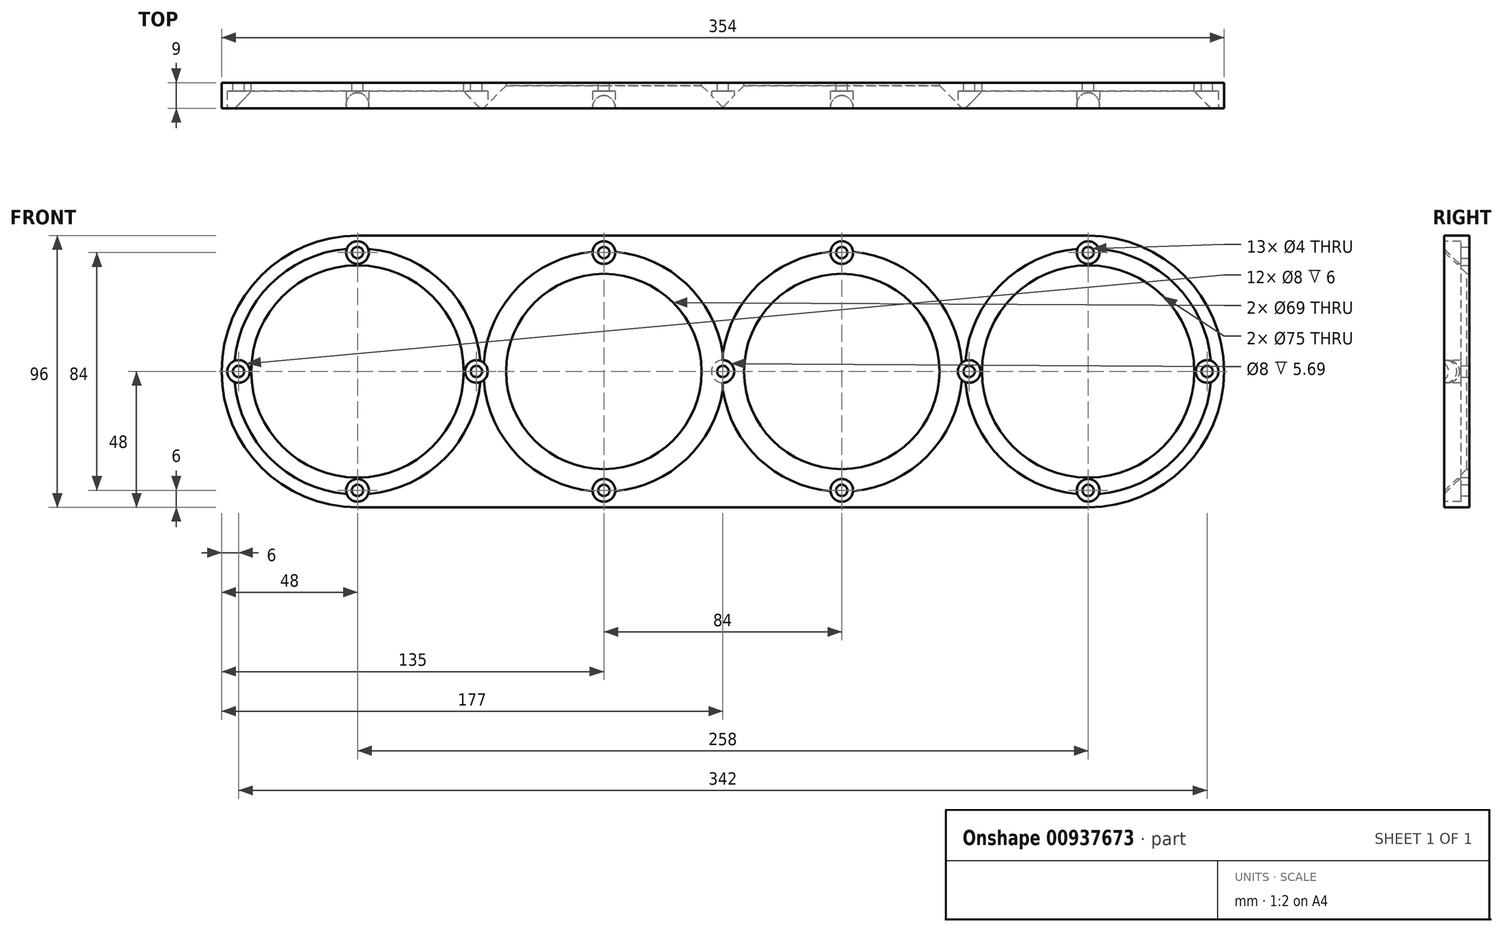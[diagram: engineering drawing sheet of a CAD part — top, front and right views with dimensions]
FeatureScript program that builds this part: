
annotation { "Feature Type Name" : "Feature", "Feature Type Description" : "" }
export const myFeature = defineFeature(function(context is Context, id is Id, definition is map)
    precondition{}
    {
        {
            var Q0;
            Q0=qCreatedBy(makeId("Front.planeOp"),FACE);
            var sketch = newSketch(context, id + "F0", { "sketchPlane" : qUnion([Q0])});
            skCircle(sketch, "E0", {"center": v(42, 0) * mm, "radius": 34.5 * mm});
            skCircle(sketch, "E1", {"center": v(129, 0) * mm, "radius": 37.5 * mm});
            skLineSegment(sketch, "E2", {"start": v(0, -113.77) * mm, "end": v(0, 113.17) * mm, "construction": true});
            skArc(sketch, "E3", {"start": v(129, 48) * mm, "mid": v(177, 0) * mm, "end": v(129, -48) * mm});
            skLineSegment(sketch, "E4", {"start": v(129, -48) * mm, "end": v(0, -48) * mm});
            skLineSegment(sketch, "E5", {"start": v(129, 48) * mm, "end": v(0, 48) * mm});
            skLineSegment(sketch, "E6.MirrorCS", {"start": v(-129, -48) * mm, "end": v(0, -48) * mm});
            skLineSegment(sketch, "E7.MirrorCS", {"start": v(-129, 48) * mm, "end": v(0, 48) * mm});
            skArc(sketch, "E8.MirrorCS", {"start": v(-129, 48) * mm, "mid": v(-177, 0) * mm, "end": v(-129, -48) * mm});
            skCircle(sketch, "E9.MirrorC", {"center": v(-129, 0) * mm, "radius": 37.5 * mm});
            skCircle(sketch, "E10.MirrorC", {"center": v(-42, 0) * mm, "radius": 34.5 * mm});
            skCircle(sketch, "E11", {"center": v(129, 42) * mm, "radius": 2 * mm});
            skCircle(sketch, "E12.1.0", {"center": v(87, 0) * mm, "radius": 2 * mm});
            skCircle(sketch, "E12.2.0", {"center": v(129, -42) * mm, "radius": 2 * mm});
            skCircle(sketch, "E12.3.0", {"center": v(171, 0) * mm, "radius": 2 * mm});
            skCircle(sketch, "E13.MirrorC", {"center": v(-171, 0) * mm, "radius": 2 * mm});
            skCircle(sketch, "E14.MirrorC", {"center": v(-129, 42) * mm, "radius": 2 * mm});
            skCircle(sketch, "E15.MirrorC", {"center": v(-129, -42) * mm, "radius": 2 * mm});
            skCircle(sketch, "E16.MirrorC", {"center": v(-87, 0) * mm, "radius": 2 * mm});
            skCircle(sketch, "E17", {"center": v(42, 42) * mm, "radius": 2 * mm});
            skCircle(sketch, "E18.1.0", {"center": v(42, -42) * mm, "radius": 2 * mm});
            skCircle(sketch, "E19.MirrorC", {"center": v(-42, 42) * mm, "radius": 2 * mm});
            skCircle(sketch, "E20.MirrorC", {"center": v(-42, -42) * mm, "radius": 2 * mm});
            skCircle(sketch, "E21", {"center": v(0, 0) * mm, "radius": 2 * mm});
            skSolve(sketch);
        }
        {
            var Q0;
            Q0 = qSketchRegion(id + "F0", true);
            extrude(context, id + "F1", {"entities" : qUnion([Q0]), "depth" : 9 * mm, "offsetDistance" : 25 * mm});
        }
        {
            var Q0;
            Q0=makeQuery(id+"F1.opExtrude","CAP_EDGE",EDGE,{"disambiguationData":[OSD([sQuery(id+"F0.wireOp",EDGE,"E0")])],"isStart":false});
            var Q1;
            Q1=makeQuery(id+"F1.opExtrude","CAP_EDGE",EDGE,{"disambiguationData":[OSD([sQuery(id+"F0.wireOp",EDGE,"E10.MirrorC")])],"isStart":false});
            chamfer(context, id + "F2", {"entities" : qUnion([Q0, Q1]), "width" : 8 * mm, "tangentPropagation" : true});
        }
        {
            var Q0;
            Q0=makeQuery(id+"F1.opExtrude","CAP_EDGE",EDGE,{"disambiguationData":[OSD([sQuery(id+"F0.wireOp",EDGE,"E1")])],"isStart":false});
            var Q1;
            Q1=makeQuery(id+"F1.opExtrude","CAP_EDGE",EDGE,{"disambiguationData":[OSD([sQuery(id+"F0.wireOp",EDGE,"E9.MirrorC")])],"isStart":false});
            chamfer(context, id + "F3", {"entities" : qUnion([Q0, Q1]), "width" : 6 * mm, "tangentPropagation" : true});
        }
        {
            var Q0;
            Q0=makeQuery(id+"F1.opExtrude","CAP_FACE",FACE,{"disambiguationData":[OSD([sQuery(id+"F0.wireOp",EDGE,"E0"),sQuery(id+"F0.wireOp",EDGE,"E1"),sQuery(id+"F0.wireOp",EDGE,"E3"),sQuery(id+"F0.wireOp",EDGE,"E4"),sQuery(id+"F0.wireOp",EDGE,"E5"),sQuery(id+"F0.wireOp",EDGE,"E6.MirrorCS"),sQuery(id+"F0.wireOp",EDGE,"E7.MirrorCS"),sQuery(id+"F0.wireOp",EDGE,"E8.MirrorCS"),sQuery(id+"F0.wireOp",EDGE,"E9.MirrorC"),sQuery(id+"F0.wireOp",EDGE,"E10.MirrorC"),sQuery(id+"F0.wireOp",EDGE,"E11"),sQuery(id+"F0.wireOp",EDGE,"E12.1.0"),sQuery(id+"F0.wireOp",EDGE,"E12.2.0"),sQuery(id+"F0.wireOp",EDGE,"E12.3.0"),sQuery(id+"F0.wireOp",EDGE,"E13.MirrorC"),sQuery(id+"F0.wireOp",EDGE,"E14.MirrorC"),sQuery(id+"F0.wireOp",EDGE,"E15.MirrorC"),sQuery(id+"F0.wireOp",EDGE,"E16.MirrorC"),sQuery(id+"F0.wireOp",EDGE,"E17"),sQuery(id+"F0.wireOp",EDGE,"E18.1.0"),sQuery(id+"F0.wireOp",EDGE,"E19.MirrorC"),sQuery(id+"F0.wireOp",EDGE,"E20.MirrorC"),sQuery(id+"F0.wireOp",EDGE,"E21")])],"isStart":false});
            var sketch = newSketch(context, id + "F4", { "sketchPlane" : qUnion([Q0])});
            skCircle(sketch, "E22", {"center": v(0, 0) * mm, "radius": 4 * mm});
            skCircle(sketch, "E23", {"center": v(42, 42) * mm, "radius": 4 * mm});
            skCircle(sketch, "E24", {"center": v(42, -42) * mm, "radius": 4 * mm});
            skCircle(sketch, "E25", {"center": v(129, 42) * mm, "radius": 4 * mm});
            skCircle(sketch, "E26.1.0", {"center": v(87, 0) * mm, "radius": 4 * mm});
            skCircle(sketch, "E26.2.0", {"center": v(129, -42) * mm, "radius": 4 * mm});
            skCircle(sketch, "E26.3.0", {"center": v(171, 0) * mm, "radius": 4 * mm});
            skPoint(sketch, "E26.center", {"position": v(129, 0) * mm});
            skLineSegment(sketch, "E27", {"start": v(0, 65.68) * mm, "end": v(0, -63.83) * mm, "construction": true});
            skPoint(sketch, "E27.endSnap0", {"position": v(0, -48) * mm});
            skCircle(sketch, "E28.MirrorC", {"center": v(-42, 42) * mm, "radius": 4 * mm});
            skCircle(sketch, "E29.MirrorC", {"center": v(-42, -42) * mm, "radius": 4 * mm});
            skCircle(sketch, "E30.MirrorC", {"center": v(-87, 0) * mm, "radius": 4 * mm});
            skCircle(sketch, "E31.MirrorC", {"center": v(-129, -42) * mm, "radius": 4 * mm});
            skCircle(sketch, "E32.MirrorC", {"center": v(-129, 42) * mm, "radius": 4 * mm});
            skCircle(sketch, "E33.MirrorC", {"center": v(-171, 0) * mm, "radius": 4 * mm});
            skSolve(sketch);
        }
        {
            var Q0;
            Q0 = qSketchRegion(id + "F4", true);
            extrude(context, id + "F5", {"entities" : qUnion([Q0]), "operationType" : NewBodyOperationType.REMOVE, "oppositeDirection" : true, "depth" : 6 * mm, "offsetDistance" : 25 * mm});
        }
    });
